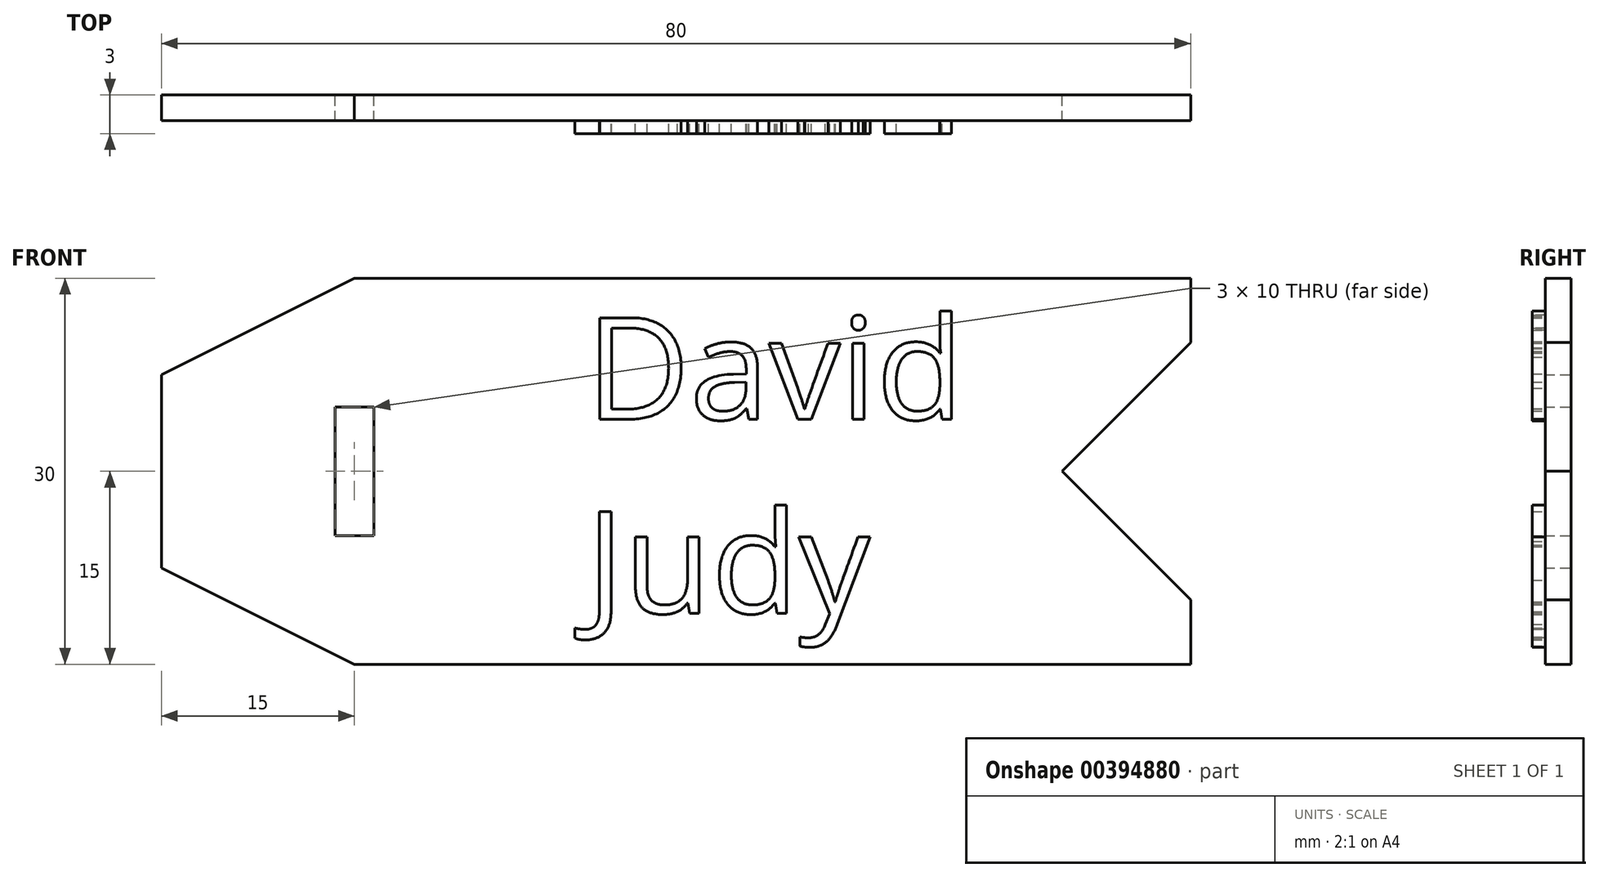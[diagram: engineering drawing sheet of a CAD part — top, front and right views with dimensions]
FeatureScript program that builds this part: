
annotation { "Feature Type Name" : "Feature", "Feature Type Description" : "" }
export const myFeature = defineFeature(function(context is Context, id is Id, definition is map)
    precondition{}
    {
        {
            var Q0;
            Q0=qCreatedBy(makeId("Front.planeOp"),FACE);
            var sketch = newSketch(context, id + "F0", { "sketchPlane" : qUnion([Q0])});
            skLineSegment(sketch, "E0.bottom", {"start": v(40, -15) * mm, "end": v(-40, -15) * mm});
            skLineSegment(sketch, "E0.top", {"start": v(40, 15) * mm, "end": v(-40, 15) * mm});
            skLineSegment(sketch, "E0.left", {"start": v(40, -15) * mm, "end": v(40, 15) * mm});
            skLineSegment(sketch, "E0.right", {"start": v(-40, -15) * mm, "end": v(-40, 15) * mm});
            skPoint(sketch, "E0.middle", {"position": v(0, 0) * mm});
            skPoint(sketch, "E1", {"position": v(-40, 7.5) * mm});
            skPoint(sketch, "E2", {"position": v(-40, -7.5) * mm});
            skPoint(sketch, "E3", {"position": v(-25, 15) * mm});
            skPoint(sketch, "E4", {"position": v(-25, -15) * mm});
            skLineSegment(sketch, "E5", {"start": v(-40, 7.5) * mm, "end": v(-25, 15) * mm});
            skLineSegment(sketch, "E6", {"start": v(-40, -7.5) * mm, "end": v(-25, -15) * mm});
            skPoint(sketch, "E7", {"position": v(-25, 0) * mm});
            skLineSegment(sketch, "E8.bottom", {"start": v(-23.5, -5) * mm, "end": v(-26.5, -5) * mm});
            skLineSegment(sketch, "E8.top", {"start": v(-23.5, 5) * mm, "end": v(-26.5, 5) * mm});
            skLineSegment(sketch, "E8.left", {"start": v(-23.5, -5) * mm, "end": v(-23.5, 5) * mm});
            skLineSegment(sketch, "E8.right", {"start": v(-26.5, -5) * mm, "end": v(-26.5, 5) * mm});
            skPoint(sketch, "E9", {"position": v(40, 0) * mm});
            skPoint(sketch, "E10", {"position": v(40, 10) * mm});
            skPoint(sketch, "E11", {"position": v(40, -10) * mm});
            skPoint(sketch, "E12", {"position": v(30, 0) * mm});
            skLineSegment(sketch, "E13", {"start": v(40, 10) * mm, "end": v(30, 0) * mm});
            skLineSegment(sketch, "E14", {"start": v(40, -10) * mm, "end": v(30, 0) * mm});
            skSolve(sketch);
        }
        {
            var Q0;
            {var subQ0=sQuery(id+"F0.wireOp",EDGE,"E5");Q0=makeQuery(id+"F0.imprint","IMPRINT",FACE,{"disambiguationData":[TD([[makeQuery(id+"F0.imprint","IMPRINT",EDGE,{"derivedFrom":subQ0}),-1.0]])]});}
            extrude(context, id + "F1", {"entities" : qUnion([Q0]), "depth" : 2 * mm});
        }
        {
            var Q0;
            Q0=makeQuery(id+"F1.opExtrude","CAP_FACE",FACE,{"disambiguationData":[OSD([sQuery(id+"F0.wireOp",EDGE,"E0.bottom"),sQuery(id+"F0.wireOp",EDGE,"E0.top"),sQuery(id+"F0.wireOp",EDGE,"E0.left"),sQuery(id+"F0.wireOp",EDGE,"E0.right"),sQuery(id+"F0.wireOp",EDGE,"E5"),sQuery(id+"F0.wireOp",EDGE,"E6"),sQuery(id+"F0.wireOp",EDGE,"E8.bottom"),sQuery(id+"F0.wireOp",EDGE,"E8.top"),sQuery(id+"F0.wireOp",EDGE,"E8.left"),sQuery(id+"F0.wireOp",EDGE,"E8.right"),sQuery(id+"F0.wireOp",EDGE,"UMAF8eoo-JTII-kxtG-y7Qu-X2FkpslPIZWo")])],"isStart":false});
            var sketch = newSketch(context, id + "F2", { "sketchPlane" : qUnion([Q0])});
            skText(sketch, "E15", { "text": "David\nJudy", "fontName": "OpenSans-Regular.ttf"});
            const initialGuessF2  = {"E15": [-0.007, 0.00403, 1, 0, 0.00797]};
            skSetInitialGuess(sketch, initialGuessF2);
            skSolve(sketch);
        }
        {
            var Q0;
            Q0 = qSketchRegion(id + "F2", true);
            extrude(context, id + "F3", {"entities" : qUnion([Q0]), "operationType" : NewBodyOperationType.ADD, "depth" : 1 * mm});
        }
    });
